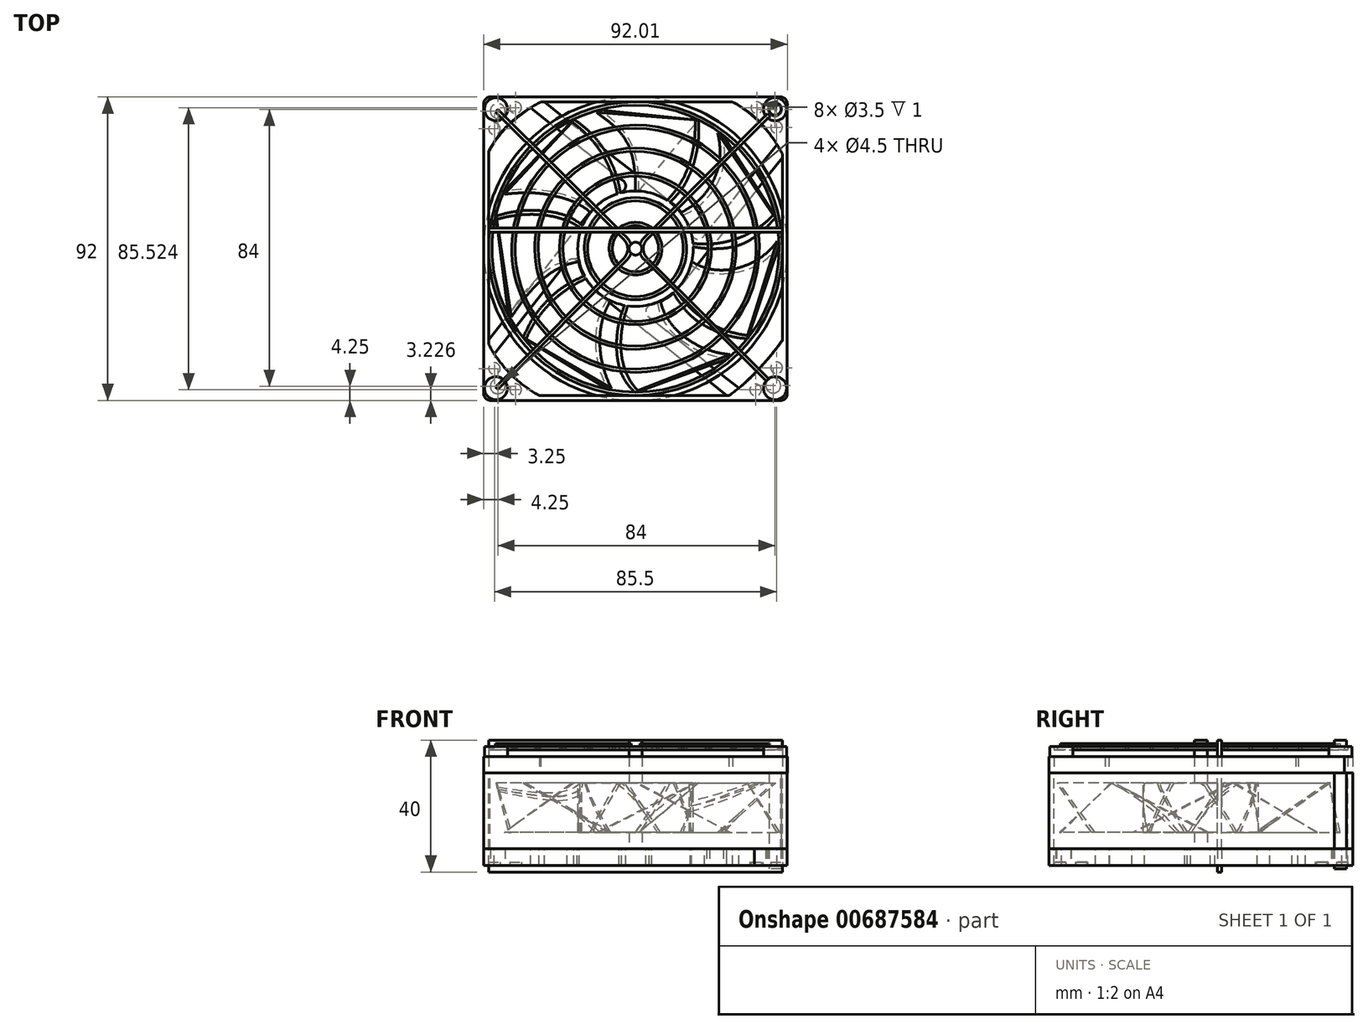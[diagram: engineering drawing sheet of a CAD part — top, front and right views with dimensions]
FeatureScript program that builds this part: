
annotation { "Feature Type Name" : "Feature", "Feature Type Description" : "" }
export const myFeature = defineFeature(function(context is Context, id is Id, definition is map)
    precondition{}
    {
        {
            var Q0;
            Q0=qCreatedBy(makeId("Top.planeOp"),FACE);
            var sketch = newSketch(context, id + "F0", { "sketchPlane" : qUnion([Q0])});
            skCircle(sketch, "E0", {"center": v(0, 0) * mm, "radius": 17.5 * mm});
            skFitSpline(sketch, "E1", {"points": [v(0, 17.5) * mm, v(-2.1, 31.24) * mm, v(-11.86, 41.33) * mm], "startDerivative": vector(0, 25.96) * mm, "endDerivative": vector(-26.51, 18.2) * mm});
            skFitSpline(sketch, "E2", {"points": [v(-13.7, 10.9) * mm, v(-25.14, 16.14) * mm, v(-39.7, 16.51) * mm], "startDerivative": vector(-17.17, 18.07) * mm, "endDerivative": vector(-36.07, -4.22) * mm});
            skFitSpline(sketch, "E3", {"points": [v(-17.05, -3.92) * mm, v(-37.64, -20.79) * mm], "startDerivative": vector(-28.13, -4.14) * mm, "endDerivative": vector(-14.48, -22.43) * mm});
            skFitSpline(sketch, "E4", {"points": [v(-7.55, -15.79) * mm, v(-7.23, -42.39) * mm], "startDerivative": vector(-14.78, -23.74) * mm, "endDerivative": vector(12.49, -22.98) * mm});
            skFitSpline(sketch, "E5", {"points": [v(7.55, -15.79) * mm, v(28.62, -32.1) * mm], "startDerivative": vector(6.16, -28.74) * mm, "endDerivative": vector(26.76, -2.2) * mm});
            skFitSpline(sketch, "E6", {"points": [v(17.05, -3.92) * mm, v(42.94, 2.35) * mm], "startDerivative": vector(28.81, -18.04) * mm, "endDerivative": vector(12.95, 20.22) * mm});
            skFitSpline(sketch, "E7", {"points": [v(13.7, 10.9) * mm, v(24.9, 35.05) * mm], "startDerivative": vector(22.05, 10.85) * mm, "endDerivative": vector(-8.83, 36.13) * mm});
            skFitSpline(sketch, "E8.0", {"points": [v(14.13, 10) * mm, v(16.05, 10.95) * mm, v(19.82, 13.47) * mm, v(24.37, 19.05) * mm, v(26.92, 26.33) * mm, v(26.64, 32.16) * mm, v(25.88, 35.29) * mm]});
            skFitSpline(sketch, "E9.0", {"points": [v(16.52, -4.77) * mm, v(17.8, -5.57) * mm, v(20.42, -6.78) * mm, v(24.46, -7.57) * mm, v(28.47, -7.48) * mm, v(33.6, -6.35) * mm, v(39.34, -3.38) * mm, v(42.62, 0) * mm, v(43.78, 1.8) * mm]});
            skFitSpline(sketch, "E10.0", {"points": [v(6.57, -16) * mm, v(7.12, -18.53) * mm, v(9.27, -23.13) * mm, v(14.71, -28.36) * mm, v(21.44, -31.83) * mm, v(26.21, -32.9) * mm, v(28.54, -33.1) * mm]});
            skFitSpline(sketch, "E11.0", {"points": [v(-8.4, -15.26) * mm, v(-9.7, -17.34) * mm, v(-11.48, -21.9) * mm, v(-12.1, -29.23) * mm, v(-10.94, -36.49) * mm, v(-9.2, -40.88) * mm, v(-8.11, -42.86) * mm]});
            skFitSpline(sketch, "E12.0", {"points": [v(-17.2, -2.94) * mm, v(-19.67, -3.3) * mm, v(-24.2, -4.9) * mm, v(-29.9, -9.15) * mm, v(-34.63, -14.5) * mm, v(-37.27, -18.36) * mm, v(-38.48, -20.24) * mm]});
            skFitSpline(sketch, "E13.0", {"points": [v(-12.97, 11.59) * mm, v(-13.75, 12.41) * mm, v(-15.56, 13.83) * mm, v(-18.2, 15.12) * mm, v(-20.4, 15.93) * mm, v(-22.1, 16.45) * mm, v(-23.77, 16.87) * mm, v(-25.42, 17.22) * mm, v(-27.03, 17.51) * mm, v(-29.17, 17.8) * mm, v(-31.91, 18) * mm, v(-35.52, 17.93) * mm, v(-38.3, 17.69) * mm, v(-39.82, 17.5) * mm]});
            skFitSpline(sketch, "E14.0", {"points": [v(1, 17.5) * mm, v(1, 18.6) * mm, v(0.97, 20.9) * mm, v(0.7, 24.59) * mm, v(0.16, 27.65) * mm, v(-0.52, 30) * mm, v(-1.18, 31.7) * mm, v(-2, 33.28) * mm, v(-3.3, 35.25) * mm, v(-5.25, 37.46) * mm, v(-8.05, 39.87) * mm, v(-10.18, 41.4) * mm, v(-11.3, 42.16) * mm]});
            skLineSegment(sketch, "E15", {"start": v(-11.3, 42.16) * mm, "end": v(-11.86, 41.33) * mm});
            skLineSegment(sketch, "E16", {"start": v(-39.82, 17.5) * mm, "end": v(-39.7, 16.51) * mm});
            skLineSegment(sketch, "E17", {"start": v(25.88, 35.29) * mm, "end": v(24.9, 35.05) * mm});
            skLineSegment(sketch, "E18", {"start": v(43.78, 1.8) * mm, "end": v(42.94, 2.35) * mm});
            skLineSegment(sketch, "E19", {"start": v(28.62, -32.1) * mm, "end": v(28.54, -33.1) * mm});
            skLineSegment(sketch, "E20", {"start": v(-8.11, -42.86) * mm, "end": v(-7.23, -42.39) * mm});
            skLineSegment(sketch, "E21", {"start": v(-38.48, -20.24) * mm, "end": v(-37.64, -20.79) * mm});
            skLineSegment(sketch, "E22", {"start": v(1, 17.5) * mm, "end": v(1, 17.47) * mm});
            skLineSegment(sketch, "E23", {"start": v(1, 17.47) * mm, "end": v(1, 17.47) * mm});
            skSolve(sketch);
        }
        {
            var Q0;
            Q0=qCreatedBy(makeId("Top.planeOp"),FACE);
            cPlane(context, id + "F1", {"entities" : qUnion([Q0]), "cplaneType" : CPlaneType.OFFSET, "offset" : 15 * mm, "width" : 150 * mm, "height" : 150 * mm});
        }
        {
            var Q0;
            Q0=qCreatedBy(id+"F1.planeOp",FACE);
            var sketch = newSketch(context, id + "F2", { "sketchPlane" : qUnion([Q0])});
            skCircle(sketch, "E24", {"center": v(0, 0) * mm, "radius": 17.5 * mm});
            skPoint(sketch, "E25", {"position": v(-17.05, -3.94) * mm});
            skPoint(sketch, "E26", {"position": v(-13.7, 10.9) * mm});
            skFitSpline(sketch, "E27", {"points": [v(-16.42, 6.06) * mm, v(-42.07, 8.89) * mm], "startDerivative": vector(-19.69, 14.9) * mm, "endDerivative": vector(-25.42, -7.54) * mm});
            skFitSpline(sketch, "E28", {"points": [v(-5.5, 16.61) * mm, v(-19.24, 38.45) * mm], "startDerivative": vector(-5.34, 25.3) * mm, "endDerivative": vector(-24.96, 18.67) * mm});
            skFitSpline(sketch, "E29", {"points": [v(9.58, 14.64) * mm, v(18.05, 39.03) * mm], "startDerivative": vector(20.74, 21.13) * mm, "endDerivative": vector(-0.95, 24.65) * mm});
            skFitSpline(sketch, "E30", {"points": [v(17.42, 1.62) * mm, v(41.76, 10.23) * mm], "startDerivative": vector(29.36, -3.55) * mm, "endDerivative": vector(17.15, 18.36) * mm});
            skFitSpline(sketch, "E31", {"points": [v(12.12, -12.62) * mm, v(34.02, -26.3) * mm], "startDerivative": vector(14.06, -21.25) * mm, "endDerivative": vector(28.38, -2.91) * mm});
            skFitSpline(sketch, "E32", {"points": [v(-2.33, -17.34) * mm, v(0.67, -43) * mm], "startDerivative": vector(-8.35, -22.6) * mm, "endDerivative": vector(20.25, -21.14) * mm});
            skFitSpline(sketch, "E33", {"points": [v(-14.96, -9.07) * mm, v(-33.19, -27.34) * mm], "startDerivative": vector(-27.43, -12.67) * mm, "endDerivative": vector(-11, -23.73) * mm});
            skFitSpline(sketch, "E34.0", {"points": [v(-4.52, 16.82) * mm, v(-4.97, 18.97) * mm, v(-6.12, 23.12) * mm, v(-8.85, 28.95) * mm, v(-12.85, 34.35) * mm, v(-16.52, 37.67) * mm, v(-18.64, 39.26) * mm]});
            skFitSpline(sketch, "E35.0", {"points": [v(10.3, 13.94) * mm, v(12.09, 15.76) * mm, v(15.01, 19.68) * mm, v(17.72, 26.07) * mm, v(19.02, 32.64) * mm, v(19.13, 36.97) * mm, v(19.05, 39.06) * mm]});
            skFitSpline(sketch, "E36.0", {"points": [v(17.3, 0.63) * mm, v(22.36, 0.02) * mm, v(32, 1.3) * mm, v(39.53, 6.38) * mm, v(42.5, 9.55) * mm]});
            skFitSpline(sketch, "E37.0", {"points": [v(11.29, -13.17) * mm, v(13.7, -16.83) * mm, v(18.5, -21.74) * mm, v(26.8, -25.94) * mm, v(31.47, -27.04) * mm, v(33.92, -27.3) * mm]});
            skFitSpline(sketch, "E38.0", {"points": [v(-3.27, -17) * mm, v(-3.98, -18.94) * mm, v(-5.18, -23.26) * mm, v(-5.71, -30.4) * mm, v(-4.4, -37.55) * mm, v(-1.84, -41.82) * mm, v(-0.05, -43.69) * mm]});
            skFitSpline(sketch, "E39.0", {"points": [v(-15.38, -8.17) * mm, v(-17.72, -9.25) * mm, v(-21.93, -11.66) * mm, v(-27.02, -16.01) * mm, v(-31.06, -21.08) * mm, v(-33.16, -24.9) * mm, v(-34.1, -26.92) * mm]});
            skFitSpline(sketch, "E40.0", {"points": [v(-15.82, 6.85) * mm, v(-17.55, 8.17) * mm, v(-21.54, 10.17) * mm, v(-28.39, 11.51) * mm, v(-35.55, 11.4) * mm, v(-40.18, 10.5) * mm, v(-42.36, 9.84) * mm]});
            skLineSegment(sketch, "E41", {"start": v(-42.36, 9.84) * mm, "end": v(-42.07, 8.89) * mm});
            skLineSegment(sketch, "E42", {"start": v(-18.64, 39.26) * mm, "end": v(-19.24, 38.45) * mm});
            skLineSegment(sketch, "E43", {"start": v(18.05, 39.03) * mm, "end": v(19.05, 39.06) * mm});
            skLineSegment(sketch, "E44", {"start": v(41.76, 10.23) * mm, "end": v(42.5, 9.55) * mm});
            skLineSegment(sketch, "E45", {"start": v(34.02, -26.3) * mm, "end": v(33.92, -27.3) * mm});
            skLineSegment(sketch, "E46", {"start": v(-0.05, -43.69) * mm, "end": v(0.67, -43) * mm});
            skLineSegment(sketch, "E47", {"start": v(-34.1, -26.92) * mm, "end": v(-33.19, -27.34) * mm});
            skSolve(sketch);
        }
        {
            var Q0;
            {var subQ0=sQuery(id+"F0.wireOp",EDGE,"E0");var subQ8=makeQuery(id+"F0.imprint","INTERSECT",VERTEX,{"derivedFrom":[subQ0,sQuery(id+"F0.wireOp",EDGE,"E7")]});Q0=makeQuery(id+"F0.imprint","IMPRINT",FACE,{"disambiguationData":[TD([[makeQuery(id+"F0.imprint","IMPRINT",EDGE,{"disambiguationData":[TD([[subQ8,1.0]])],"derivedFrom":subQ0}),1.0]])]});}
            var Q1;
            {var subQ0=sQuery(id+"F2.wireOp",EDGE,"E24");var subQ8=makeQuery(id+"F2.imprint","INTERSECT",VERTEX,{"derivedFrom":[subQ0,sQuery(id+"F2.wireOp",EDGE,"E30")]});Q1=makeQuery(id+"F2.imprint","IMPRINT",FACE,{"disambiguationData":[TD([[makeQuery(id+"F2.imprint","IMPRINT",EDGE,{"disambiguationData":[TD([[subQ8,1.0]])],"derivedFrom":subQ0}),1.0]])]});}
            loft(context, id + "F3", {"sheetProfilesArray" : [{ "sheetProfileEntities" : qUnion([Q0]) }, { "sheetProfileEntities" : qUnion([Q1]) }]});
        }
        {
            var Q1;
            {var subQ0=sQuery(id+"F2.wireOp",EDGE,"E27");Q1=makeQuery(id+"F2.imprint","IMPRINT",FACE,{"disambiguationData":[TD([[makeQuery(id+"F2.imprint","IMPRINT",EDGE,{"derivedFrom":subQ0}),-1.0]])]});}
            var Q2;
            {var subQ0=sQuery(id+"F0.wireOp",EDGE,"E3");Q2=makeQuery(id+"F0.imprint","IMPRINT",FACE,{"disambiguationData":[TD([[makeQuery(id+"F0.imprint","IMPRINT",EDGE,{"derivedFrom":subQ0}),-1.0]])]});}
            loft(context, id + "F4", {"operationType" : NewBodyOperationType.ADD, "sheetProfilesArray" : [{ "sheetProfileEntities" : qUnion([Q1]) }, { "sheetProfileEntities" : qUnion([Q2]) }]});
        }
        {
            var Q1;
            {var subQ0=sQuery(id+"F2.wireOp",EDGE,"E28");Q1=makeQuery(id+"F2.imprint","IMPRINT",FACE,{"disambiguationData":[TD([[makeQuery(id+"F2.imprint","IMPRINT",EDGE,{"derivedFrom":subQ0}),-1.0]])]});}
            var Q2;
            {var subQ0=sQuery(id+"F0.wireOp",EDGE,"E2");Q2=makeQuery(id+"F0.imprint","IMPRINT",FACE,{"disambiguationData":[TD([[makeQuery(id+"F0.imprint","IMPRINT",EDGE,{"derivedFrom":subQ0}),-1.0]])]});}
            loft(context, id + "F5", {"operationType" : NewBodyOperationType.ADD, "sheetProfilesArray" : [{ "sheetProfileEntities" : qUnion([Q1]) }, { "sheetProfileEntities" : qUnion([Q2]) }]});
        }
        {
            var Q1;
            {var subQ0=sQuery(id+"F2.wireOp",EDGE,"E33");Q1=makeQuery(id+"F2.imprint","IMPRINT",FACE,{"disambiguationData":[TD([[makeQuery(id+"F2.imprint","IMPRINT",EDGE,{"derivedFrom":subQ0}),-1.0]])]});}
            var Q2;
            {var subQ0=sQuery(id+"F0.wireOp",EDGE,"E4");Q2=makeQuery(id+"F0.imprint","IMPRINT",FACE,{"disambiguationData":[TD([[makeQuery(id+"F0.imprint","IMPRINT",EDGE,{"derivedFrom":subQ0}),-1.0]])]});}
            loft(context, id + "F6", {"operationType" : NewBodyOperationType.ADD, "sheetProfilesArray" : [{ "sheetProfileEntities" : qUnion([Q1]) }, { "sheetProfileEntities" : qUnion([Q2]) }]});
        }
        {
            var Q1;
            {var subQ0=sQuery(id+"F0.wireOp",EDGE,"E1");Q1=makeQuery(id+"F0.imprint","IMPRINT",FACE,{"disambiguationData":[TD([[makeQuery(id+"F0.imprint","IMPRINT",EDGE,{"derivedFrom":subQ0}),-1.0]])]});}
            var Q2;
            {var subQ0=sQuery(id+"F2.wireOp",EDGE,"E29");Q2=makeQuery(id+"F2.imprint","IMPRINT",FACE,{"disambiguationData":[TD([[makeQuery(id+"F2.imprint","IMPRINT",EDGE,{"derivedFrom":subQ0}),-1.0]])]});}
            loft(context, id + "F7", {"operationType" : NewBodyOperationType.ADD, "sheetProfilesArray" : [{ "sheetProfileEntities" : qUnion([Q1]) }, { "sheetProfileEntities" : qUnion([Q2]) }]});
        }
        {
            var Q1;
            {var subQ0=sQuery(id+"F0.wireOp",EDGE,"E7");Q1=makeQuery(id+"F0.imprint","IMPRINT",FACE,{"disambiguationData":[TD([[makeQuery(id+"F0.imprint","IMPRINT",EDGE,{"derivedFrom":subQ0}),-1.0]])]});}
            var Q2;
            {var subQ0=sQuery(id+"F2.wireOp",EDGE,"E30");Q2=makeQuery(id+"F2.imprint","IMPRINT",FACE,{"disambiguationData":[TD([[makeQuery(id+"F2.imprint","IMPRINT",EDGE,{"derivedFrom":subQ0}),-1.0]])]});}
            loft(context, id + "F8", {"operationType" : NewBodyOperationType.ADD, "sheetProfilesArray" : [{ "sheetProfileEntities" : qUnion([Q1]) }, { "sheetProfileEntities" : qUnion([Q2]) }]});
        }
        {
            var Q1;
            {var subQ0=sQuery(id+"F0.wireOp",EDGE,"E6");Q1=makeQuery(id+"F0.imprint","IMPRINT",FACE,{"disambiguationData":[TD([[makeQuery(id+"F0.imprint","IMPRINT",EDGE,{"derivedFrom":subQ0}),-1.0]])]});}
            var Q2;
            {var subQ0=sQuery(id+"F2.wireOp",EDGE,"E31");Q2=makeQuery(id+"F2.imprint","IMPRINT",FACE,{"disambiguationData":[TD([[makeQuery(id+"F2.imprint","IMPRINT",EDGE,{"derivedFrom":subQ0}),-1.0]])]});}
            loft(context, id + "F9", {"operationType" : NewBodyOperationType.ADD, "sheetProfilesArray" : [{ "sheetProfileEntities" : qUnion([Q1]) }, { "sheetProfileEntities" : qUnion([Q2]) }]});
        }
        {
            var Q1;
            {var subQ0=sQuery(id+"F0.wireOp",EDGE,"E5");Q1=makeQuery(id+"F0.imprint","IMPRINT",FACE,{"disambiguationData":[TD([[makeQuery(id+"F0.imprint","IMPRINT",EDGE,{"derivedFrom":subQ0}),-1.0]])]});}
            var Q2;
            {var subQ0=sQuery(id+"F2.wireOp",EDGE,"E32");Q2=makeQuery(id+"F2.imprint","IMPRINT",FACE,{"disambiguationData":[TD([[makeQuery(id+"F2.imprint","IMPRINT",EDGE,{"derivedFrom":subQ0}),-1.0]])]});}
            loft(context, id + "F10", {"operationType" : NewBodyOperationType.ADD, "sheetProfilesArray" : [{ "sheetProfileEntities" : qUnion([Q1]) }, { "sheetProfileEntities" : qUnion([Q2]) }]});
        }
        {
            var Q0;
            Q0=qCreatedBy(makeId("Top.planeOp"),FACE);
            cPlane(context, id + "F11", {"entities" : qUnion([Q0]), "cplaneType" : CPlaneType.OFFSET, "offset" : 5 * mm, "oppositeDirection" : true, "width" : 150 * mm, "height" : 150 * mm});
        }
        {
            var Q0;
            Q0=qCreatedBy(id+"F11.planeOp",FACE);
            var sketch = newSketch(context, id + "F12", { "sketchPlane" : qUnion([Q0])});
            skArc(sketch, "E48", {"start": v(4.24, -17.24) * mm, "mid": v(9.6, -14.93) * mm, "end": v(13.92, -11.01) * mm});
            skLineSegment(sketch, "E49", {"start": v(36, -46) * mm, "end": v(44.08, -45.69) * mm});
            skLineSegment(sketch, "E50", {"start": v(46, -43.69) * mm, "end": v(46, 44) * mm});
            skLineSegment(sketch, "E51", {"start": v(36, -46) * mm, "end": v(-44, -46) * mm});
            skLineSegment(sketch, "E52", {"start": v(-46, -44) * mm, "end": v(-46, 44) * mm});
            skLineSegment(sketch, "E53", {"start": v(-44, 46) * mm, "end": v(26, 46) * mm});
            skPoint(sketch, "E54.endSnap0", {"position": v(0, 46) * mm});
            skLineSegment(sketch, "E55", {"start": v(27.65, -44.5) * mm, "end": v(-11.01, -13.92) * mm});
            skLineSegment(sketch, "E56", {"start": v(31.31, -42.3) * mm, "end": v(3.54, -20.33) * mm});
            skArc(sketch, "E57", {"start": v(4.9, -17.06) * mm, "mid": v(3.11, -18.68) * mm, "end": v(4.2, -20.84) * mm});
            skLineSegment(sketch, "E58", {"start": v(44.5, 27.65) * mm, "end": v(13.92, -11.01) * mm});
            skArc(sketch, "E59", {"start": v(17.02, 5.05) * mm, "mid": v(18.63, 2.88) * mm, "end": v(20.93, 4.3) * mm});
            skArc(sketch, "E60.trimOffspring", {"start": v(17.36, 3.72) * mm, "mid": v(15.07, 9.37) * mm, "end": v(11.01, 13.92) * mm});
            skLineSegment(sketch, "E61", {"start": v(-27.65, 44.5) * mm, "end": v(11.01, 13.92) * mm});
            skLineSegment(sketch, "E62", {"start": v(-31.83, 42.7) * mm, "end": v(-3.31, 20.15) * mm});
            skPoint(sketch, "E63.orphan", {"position": v(-32, 47.94) * mm});
            skArc(sketch, "E64", {"start": v(-4.95, 17.05) * mm, "mid": v(-3, 18.71) * mm, "end": v(-4.3, 20.92) * mm});
            skArc(sketch, "E65.trimOffspring", {"start": v(-4.03, 17.29) * mm, "mid": v(-9.5, 14.99) * mm, "end": v(-13.92, 11.01) * mm});
            skLineSegment(sketch, "E66", {"start": v(-44.5, -27.65) * mm, "end": v(-13.92, 11.01) * mm});
            skLineSegment(sketch, "E67", {"start": v(-42.8, -31.95) * mm, "end": v(-20.44, -3.69) * mm});
            skPoint(sketch, "E68.orphan", {"position": v(-47.94, -32) * mm});
            skArc(sketch, "E69", {"start": v(-17.06, -4.88) * mm, "mid": v(-18.63, -3.16) * mm, "end": v(-20.77, -4.1) * mm});
            skArc(sketch, "E70.trimOffspring", {"start": v(-17.21, -4.33) * mm, "mid": v(-14.9, -9.64) * mm, "end": v(-11.01, -13.92) * mm});
            skPoint(sketch, "E71.orphan", {"position": v(-46, 0) * mm});
            skPoint(sketch, "E54.end.orphan", {"position": v(0, 46) * mm});
            skLineSegment(sketch, "E72.0", {"start": v(44.5, -27.75) * mm, "end": v(44.5, 27.65) * mm});
            skLineSegment(sketch, "E72.1", {"start": v(-27.65, 44.5) * mm, "end": v(29.37, 44.5) * mm});
            skLineSegment(sketch, "E72.2", {"start": v(-44.5, -27.65) * mm, "end": v(-44.5, 29.38) * mm});
            skLineSegment(sketch, "E72.3", {"start": v(0, -44.5) * mm, "end": v(-29.19, -44.5) * mm});
            skLineSegment(sketch, "E73", {"start": v(-46, 44) * mm, "end": v(-46, 26) * mm});
            skLineSegment(sketch, "E74", {"start": v(-44, 46) * mm, "end": v(-29.55, 46) * mm});
            skFitSpline(sketch, "E75", {"points": [v(-46, 26) * mm, v(-26, 46) * mm], "startDerivative": vector(10.96, 29.27) * mm, "endDerivative": vector(25.62, 12.75) * mm});
            skPoint(sketch, "E76.orphan", {"position": v(-36, 46) * mm});
            skPoint(sketch, "E77.visualSharp", {"position": v(-46, 46) * mm});
            skArc(sketch, "E77.filletArc", {"start": v(-44, 46) * mm, "mid": v(-45.41, 45.41) * mm, "end": v(-46, 44) * mm});
            skPoint(sketch, "E78.visualSharp", {"position": v(-46, -46) * mm});
            skArc(sketch, "E78.filletArc", {"start": v(-46, -44) * mm, "mid": v(-45.41, -45.41) * mm, "end": v(-44, -46) * mm});
            skLineSegment(sketch, "E79", {"start": v(0, -44.5) * mm, "end": v(27.65, -44.5) * mm});
            skPoint(sketch, "E80.visualSharp", {"position": v(46, -45.61) * mm});
            skArc(sketch, "E80.filletArc", {"start": v(44.08, -45.69) * mm, "mid": v(45.44, -45.08) * mm, "end": v(46, -43.69) * mm});
            skPoint(sketch, "E81.visualSharp", {"position": v(46, 46) * mm});
            skArc(sketch, "E81.filletArc", {"start": v(46, 44) * mm, "mid": v(45.41, 45.41) * mm, "end": v(44, 46) * mm});
            skPoint(sketch, "E82.orphan", {"position": v(-46, -36) * mm});
            skLineSegment(sketch, "E83", {"start": v(-46, -44) * mm, "end": v(-46, -26) * mm});
            skLineSegment(sketch, "E84", {"start": v(-44, -46) * mm, "end": v(-26, -46) * mm});
            skFitSpline(sketch, "E85", {"points": [v(-46, -26) * mm, v(-26, -46) * mm], "startDerivative": vector(11.48, -26.33) * mm, "endDerivative": vector(28, -11.54) * mm});
            skLineSegment(sketch, "E86", {"start": v(46, -43.69) * mm, "end": v(46, -25.61) * mm});
            skLineSegment(sketch, "E87", {"start": v(44.08, -45.69) * mm, "end": v(36, -46) * mm});
            skFitSpline(sketch, "E88", {"points": [v(26, -46.39) * mm, v(46, -25.61) * mm], "startDerivative": vector(23.59, 16.36) * mm, "endDerivative": vector(17.03, 24.93) * mm});
            skPoint(sketch, "E89.orphan", {"position": v(36, -46) * mm});
            skLineSegment(sketch, "E90", {"start": v(44, 46) * mm, "end": v(26, 46) * mm});
            skLineSegment(sketch, "E91", {"start": v(46, 44) * mm, "end": v(46, 26) * mm});
            skFitSpline(sketch, "E92", {"points": [v(26, 46) * mm, v(46, 26) * mm], "startDerivative": vector(29.17, -10.7) * mm, "endDerivative": vector(10.2, -22.47) * mm});
            skLineSegment(sketch, "E93.trimOffspring", {"start": v(42.91, 31.62) * mm, "end": v(19.98, 3.1) * mm});
            skPoint(sketch, "E94.start.orphan", {"position": v(46, 36) * mm});
            skSolve(sketch);
        }
        {
            var Q0;
            {var subQ24=sQuery(id+"F12.wireOp",EDGE,"E55");Q0=makeQuery(id+"F12.imprint","IMPRINT",FACE,{"disambiguationData":[TD([[makeQuery(id+"F12.imprint","IMPRINT",EDGE,{"derivedFrom":subQ24}),-1.0]])]});}
            extrude(context, id + "F13", {"entities" : qUnion([Q0]), "operationType" : NewBodyOperationType.ADD, "oppositeDirection" : true, "depth" : 5 * mm, "offsetDistance" : 25 * mm});
        }
        {
            var Q0;
            Q0 = qSketchRegion(id + "F12", true);
            extrude(context, id + "F14", {"entities" : qUnion([Q0]), "oppositeDirection" : true, "depth" : 5 * mm, "offsetDistance" : 25 * mm});
        }
        {
            var Q0;
            Q0=makeQuery(id+"F13.opExtrude","CAP_FACE",FACE,{"disambiguationData":[OSD([sQuery(id+"F12.wireOp",EDGE,"E48"),sQuery(id+"F12.wireOp",EDGE,"E50"),sQuery(id+"F12.wireOp",EDGE,"E51"),sQuery(id+"F12.wireOp",EDGE,"E52"),sQuery(id+"F12.wireOp",EDGE,"E53"),sQuery(id+"F12.wireOp",EDGE,"E55"),sQuery(id+"F12.wireOp",EDGE,"E56"),sQuery(id+"F12.wireOp",EDGE,"E57"),sQuery(id+"F12.wireOp",EDGE,"E58"),sQuery(id+"F12.wireOp",EDGE,"E59"),sQuery(id+"F12.wireOp",EDGE,"E60.trimOffspring"),sQuery(id+"F12.wireOp",EDGE,"E61"),sQuery(id+"F12.wireOp",EDGE,"E62"),sQuery(id+"F12.wireOp",EDGE,"E64"),sQuery(id+"F12.wireOp",EDGE,"E65.trimOffspring"),sQuery(id+"F12.wireOp",EDGE,"E66"),sQuery(id+"F12.wireOp",EDGE,"E67"),sQuery(id+"F12.wireOp",EDGE,"E69"),sQuery(id+"F12.wireOp",EDGE,"E70.trimOffspring"),sQuery(id+"F12.wireOp",EDGE,"E72.0"),sQuery(id+"F12.wireOp",EDGE,"E72.1"),sQuery(id+"F12.wireOp",EDGE,"E72.2"),sQuery(id+"F12.wireOp",EDGE,"E72.3"),sQuery(id+"F12.wireOp",EDGE,"E73"),sQuery(id+"F12.wireOp",EDGE,"E74"),sQuery(id+"F12.wireOp",EDGE,"E75"),sQuery(id+"F12.wireOp",EDGE,"E77.filletArc"),sQuery(id+"F12.wireOp",EDGE,"E78.filletArc"),sQuery(id+"F12.wireOp",EDGE,"E79"),sQuery(id+"F12.wireOp",EDGE,"E80.filletArc"),sQuery(id+"F12.wireOp",EDGE,"E81.filletArc"),sQuery(id+"F12.wireOp",EDGE,"E83"),sQuery(id+"F12.wireOp",EDGE,"E84"),sQuery(id+"F12.wireOp",EDGE,"E85"),sQuery(id+"F12.wireOp",EDGE,"E86"),sQuery(id+"F12.wireOp",EDGE,"E87"),sQuery(id+"F12.wireOp",EDGE,"E90"),sQuery(id+"F12.wireOp",EDGE,"E91"),sQuery(id+"F12.wireOp",EDGE,"E92"),sQuery(id+"F12.wireOp",EDGE,"E93.trimOffspring"),sQuery(id+"F12.wireOp",EDGE,"E88")])],"isStart":false});
            var sketch = newSketch(context, id + "F15", { "sketchPlane" : qUnion([Q0])});
            skCircle(sketch, "E95", {"center": v(-41.75, -41.75) * mm, "radius": 2.25 * mm});
            skSolve(sketch);
        }
        {
            var Q0;
            Q0 = qSketchRegion(id + "F15", true);
            extrude(context, id + "F16", {"entities" : qUnion([Q0]), "operationType" : NewBodyOperationType.REMOVE, "endBound" : BoundingType.THROUGH_ALL, "oppositeDirection" : true, "depth" : 25 * mm, "offsetDistance" : 25 * mm});
        }
        {
            var Q0;
            Q0=makeQuery(id+"F13.opExtrude","CAP_FACE",FACE,{"disambiguationData":[OSD([sQuery(id+"F12.wireOp",EDGE,"E48"),sQuery(id+"F12.wireOp",EDGE,"E50"),sQuery(id+"F12.wireOp",EDGE,"E51"),sQuery(id+"F12.wireOp",EDGE,"E52"),sQuery(id+"F12.wireOp",EDGE,"E53"),sQuery(id+"F12.wireOp",EDGE,"E55"),sQuery(id+"F12.wireOp",EDGE,"E56"),sQuery(id+"F12.wireOp",EDGE,"E57"),sQuery(id+"F12.wireOp",EDGE,"E58"),sQuery(id+"F12.wireOp",EDGE,"E59"),sQuery(id+"F12.wireOp",EDGE,"E60.trimOffspring"),sQuery(id+"F12.wireOp",EDGE,"E61"),sQuery(id+"F12.wireOp",EDGE,"E62"),sQuery(id+"F12.wireOp",EDGE,"E64"),sQuery(id+"F12.wireOp",EDGE,"E65.trimOffspring"),sQuery(id+"F12.wireOp",EDGE,"E66"),sQuery(id+"F12.wireOp",EDGE,"E67"),sQuery(id+"F12.wireOp",EDGE,"E69"),sQuery(id+"F12.wireOp",EDGE,"E70.trimOffspring"),sQuery(id+"F12.wireOp",EDGE,"E72.0"),sQuery(id+"F12.wireOp",EDGE,"E72.1"),sQuery(id+"F12.wireOp",EDGE,"E72.2"),sQuery(id+"F12.wireOp",EDGE,"E72.3"),sQuery(id+"F12.wireOp",EDGE,"E73"),sQuery(id+"F12.wireOp",EDGE,"E74"),sQuery(id+"F12.wireOp",EDGE,"E75"),sQuery(id+"F12.wireOp",EDGE,"E77.filletArc"),sQuery(id+"F12.wireOp",EDGE,"E78.filletArc"),sQuery(id+"F12.wireOp",EDGE,"E79"),sQuery(id+"F12.wireOp",EDGE,"E80.filletArc"),sQuery(id+"F12.wireOp",EDGE,"E81.filletArc"),sQuery(id+"F12.wireOp",EDGE,"E83"),sQuery(id+"F12.wireOp",EDGE,"E84"),sQuery(id+"F12.wireOp",EDGE,"E85"),sQuery(id+"F12.wireOp",EDGE,"E86"),sQuery(id+"F12.wireOp",EDGE,"E87"),sQuery(id+"F12.wireOp",EDGE,"E90"),sQuery(id+"F12.wireOp",EDGE,"E91"),sQuery(id+"F12.wireOp",EDGE,"E92"),sQuery(id+"F12.wireOp",EDGE,"E93.trimOffspring"),sQuery(id+"F12.wireOp",EDGE,"E88")])],"isStart":false});
            var sketch = newSketch(context, id + "F17", { "sketchPlane" : qUnion([Q0])});
            skCircle(sketch, "E96", {"center": v(-42.75, -36.34) * mm, "radius": 1.75 * mm});
            skSolve(sketch);
        }
        {
            var Q0;
            Q0 = qSketchRegion(id + "F17", true);
            extrude(context, id + "F18", {"entities" : qUnion([Q0]), "operationType" : NewBodyOperationType.REMOVE, "oppositeDirection" : true, "depth" : 1 * mm, "offsetDistance" : 25 * mm});
        }
        {
            var Q0;
            Q0=makeQuery(id+"F13.opExtrude","CAP_FACE",FACE,{"disambiguationData":[OSD([sQuery(id+"F12.wireOp",EDGE,"E48"),sQuery(id+"F12.wireOp",EDGE,"E50"),sQuery(id+"F12.wireOp",EDGE,"E51"),sQuery(id+"F12.wireOp",EDGE,"E52"),sQuery(id+"F12.wireOp",EDGE,"E53"),sQuery(id+"F12.wireOp",EDGE,"E55"),sQuery(id+"F12.wireOp",EDGE,"E56"),sQuery(id+"F12.wireOp",EDGE,"E57"),sQuery(id+"F12.wireOp",EDGE,"E58"),sQuery(id+"F12.wireOp",EDGE,"E59"),sQuery(id+"F12.wireOp",EDGE,"E60.trimOffspring"),sQuery(id+"F12.wireOp",EDGE,"E61"),sQuery(id+"F12.wireOp",EDGE,"E62"),sQuery(id+"F12.wireOp",EDGE,"E64"),sQuery(id+"F12.wireOp",EDGE,"E65.trimOffspring"),sQuery(id+"F12.wireOp",EDGE,"E66"),sQuery(id+"F12.wireOp",EDGE,"E67"),sQuery(id+"F12.wireOp",EDGE,"E69"),sQuery(id+"F12.wireOp",EDGE,"E70.trimOffspring"),sQuery(id+"F12.wireOp",EDGE,"E72.0"),sQuery(id+"F12.wireOp",EDGE,"E72.1"),sQuery(id+"F12.wireOp",EDGE,"E72.2"),sQuery(id+"F12.wireOp",EDGE,"E72.3"),sQuery(id+"F12.wireOp",EDGE,"E73"),sQuery(id+"F12.wireOp",EDGE,"E74"),sQuery(id+"F12.wireOp",EDGE,"E75"),sQuery(id+"F12.wireOp",EDGE,"E77.filletArc"),sQuery(id+"F12.wireOp",EDGE,"E78.filletArc"),sQuery(id+"F12.wireOp",EDGE,"E79"),sQuery(id+"F12.wireOp",EDGE,"E80.filletArc"),sQuery(id+"F12.wireOp",EDGE,"E81.filletArc"),sQuery(id+"F12.wireOp",EDGE,"E83"),sQuery(id+"F12.wireOp",EDGE,"E84"),sQuery(id+"F12.wireOp",EDGE,"E85"),sQuery(id+"F12.wireOp",EDGE,"E86"),sQuery(id+"F12.wireOp",EDGE,"E87"),sQuery(id+"F12.wireOp",EDGE,"E90"),sQuery(id+"F12.wireOp",EDGE,"E91"),sQuery(id+"F12.wireOp",EDGE,"E92"),sQuery(id+"F12.wireOp",EDGE,"E93.trimOffspring"),sQuery(id+"F12.wireOp",EDGE,"E88")])],"isStart":false});
            var sketch = newSketch(context, id + "F19", { "sketchPlane" : qUnion([Q0])});
            skCircle(sketch, "E97", {"center": v(-36.34, -42.75) * mm, "radius": 1.75 * mm});
            skSolve(sketch);
        }
        {
            var Q0;
            Q0 = qSketchRegion(id + "F19", true);
            extrude(context, id + "F20", {"entities" : qUnion([Q0]), "operationType" : NewBodyOperationType.REMOVE, "oppositeDirection" : true, "depth" : 1 * mm, "offsetDistance" : 25 * mm});
        }
        {
            var Q0;
            Q0=makeQuery(id+"F13.opExtrude","CAP_FACE",FACE,{"disambiguationData":[OSD([sQuery(id+"F12.wireOp",EDGE,"E48"),sQuery(id+"F12.wireOp",EDGE,"E50"),sQuery(id+"F12.wireOp",EDGE,"E51"),sQuery(id+"F12.wireOp",EDGE,"E52"),sQuery(id+"F12.wireOp",EDGE,"E53"),sQuery(id+"F12.wireOp",EDGE,"E55"),sQuery(id+"F12.wireOp",EDGE,"E56"),sQuery(id+"F12.wireOp",EDGE,"E57"),sQuery(id+"F12.wireOp",EDGE,"E58"),sQuery(id+"F12.wireOp",EDGE,"E59"),sQuery(id+"F12.wireOp",EDGE,"E60.trimOffspring"),sQuery(id+"F12.wireOp",EDGE,"E61"),sQuery(id+"F12.wireOp",EDGE,"E62"),sQuery(id+"F12.wireOp",EDGE,"E64"),sQuery(id+"F12.wireOp",EDGE,"E65.trimOffspring"),sQuery(id+"F12.wireOp",EDGE,"E66"),sQuery(id+"F12.wireOp",EDGE,"E67"),sQuery(id+"F12.wireOp",EDGE,"E69"),sQuery(id+"F12.wireOp",EDGE,"E70.trimOffspring"),sQuery(id+"F12.wireOp",EDGE,"E72.0"),sQuery(id+"F12.wireOp",EDGE,"E72.1"),sQuery(id+"F12.wireOp",EDGE,"E72.2"),sQuery(id+"F12.wireOp",EDGE,"E72.3"),sQuery(id+"F12.wireOp",EDGE,"E73"),sQuery(id+"F12.wireOp",EDGE,"E74"),sQuery(id+"F12.wireOp",EDGE,"E75"),sQuery(id+"F12.wireOp",EDGE,"E77.filletArc"),sQuery(id+"F12.wireOp",EDGE,"E78.filletArc"),sQuery(id+"F12.wireOp",EDGE,"E79"),sQuery(id+"F12.wireOp",EDGE,"E80.filletArc"),sQuery(id+"F12.wireOp",EDGE,"E81.filletArc"),sQuery(id+"F12.wireOp",EDGE,"E83"),sQuery(id+"F12.wireOp",EDGE,"E84"),sQuery(id+"F12.wireOp",EDGE,"E85"),sQuery(id+"F12.wireOp",EDGE,"E86"),sQuery(id+"F12.wireOp",EDGE,"E87"),sQuery(id+"F12.wireOp",EDGE,"E90"),sQuery(id+"F12.wireOp",EDGE,"E91"),sQuery(id+"F12.wireOp",EDGE,"E92"),sQuery(id+"F12.wireOp",EDGE,"E93.trimOffspring"),sQuery(id+"F12.wireOp",EDGE,"E88")])],"isStart":false});
            var sketch = newSketch(context, id + "F21", { "sketchPlane" : qUnion([Q0])});
            skCircle(sketch, "E98", {"center": v(-41.75, 41.75) * mm, "radius": 2.25 * mm});
            skSolve(sketch);
        }
        {
            var Q0;
            Q0 = qSketchRegion(id + "F21", true);
            extrude(context, id + "F22", {"entities" : qUnion([Q0]), "operationType" : NewBodyOperationType.REMOVE, "endBound" : BoundingType.THROUGH_ALL, "oppositeDirection" : true, "depth" : 25 * mm, "offsetDistance" : 25 * mm});
        }
        {
            var Q0;
            Q0=makeQuery(id+"F13.opExtrude","CAP_FACE",FACE,{"disambiguationData":[OSD([sQuery(id+"F12.wireOp",EDGE,"E48"),sQuery(id+"F12.wireOp",EDGE,"E50"),sQuery(id+"F12.wireOp",EDGE,"E51"),sQuery(id+"F12.wireOp",EDGE,"E52"),sQuery(id+"F12.wireOp",EDGE,"E53"),sQuery(id+"F12.wireOp",EDGE,"E55"),sQuery(id+"F12.wireOp",EDGE,"E56"),sQuery(id+"F12.wireOp",EDGE,"E57"),sQuery(id+"F12.wireOp",EDGE,"E58"),sQuery(id+"F12.wireOp",EDGE,"E59"),sQuery(id+"F12.wireOp",EDGE,"E60.trimOffspring"),sQuery(id+"F12.wireOp",EDGE,"E61"),sQuery(id+"F12.wireOp",EDGE,"E62"),sQuery(id+"F12.wireOp",EDGE,"E64"),sQuery(id+"F12.wireOp",EDGE,"E65.trimOffspring"),sQuery(id+"F12.wireOp",EDGE,"E66"),sQuery(id+"F12.wireOp",EDGE,"E67"),sQuery(id+"F12.wireOp",EDGE,"E69"),sQuery(id+"F12.wireOp",EDGE,"E70.trimOffspring"),sQuery(id+"F12.wireOp",EDGE,"E72.0"),sQuery(id+"F12.wireOp",EDGE,"E72.1"),sQuery(id+"F12.wireOp",EDGE,"E72.2"),sQuery(id+"F12.wireOp",EDGE,"E72.3"),sQuery(id+"F12.wireOp",EDGE,"E73"),sQuery(id+"F12.wireOp",EDGE,"E74"),sQuery(id+"F12.wireOp",EDGE,"E75"),sQuery(id+"F12.wireOp",EDGE,"E77.filletArc"),sQuery(id+"F12.wireOp",EDGE,"E78.filletArc"),sQuery(id+"F12.wireOp",EDGE,"E79"),sQuery(id+"F12.wireOp",EDGE,"E80.filletArc"),sQuery(id+"F12.wireOp",EDGE,"E81.filletArc"),sQuery(id+"F12.wireOp",EDGE,"E83"),sQuery(id+"F12.wireOp",EDGE,"E84"),sQuery(id+"F12.wireOp",EDGE,"E85"),sQuery(id+"F12.wireOp",EDGE,"E86"),sQuery(id+"F12.wireOp",EDGE,"E87"),sQuery(id+"F12.wireOp",EDGE,"E90"),sQuery(id+"F12.wireOp",EDGE,"E91"),sQuery(id+"F12.wireOp",EDGE,"E92"),sQuery(id+"F12.wireOp",EDGE,"E93.trimOffspring"),sQuery(id+"F12.wireOp",EDGE,"E88")])],"isStart":false});
            var sketch = newSketch(context, id + "F23", { "sketchPlane" : qUnion([Q0])});
            skCircle(sketch, "E99", {"center": v(-42.75, 36.34) * mm, "radius": 1.75 * mm});
            skSolve(sketch);
        }
        {
            var Q0;
            Q0 = qSketchRegion(id + "F23", true);
            extrude(context, id + "F24", {"entities" : qUnion([Q0]), "operationType" : NewBodyOperationType.REMOVE, "oppositeDirection" : true, "depth" : 1 * mm, "offsetDistance" : 25 * mm});
        }
        {
            var Q0;
            Q0=makeQuery(id+"F13.opExtrude","CAP_FACE",FACE,{"disambiguationData":[OSD([sQuery(id+"F12.wireOp",EDGE,"E48"),sQuery(id+"F12.wireOp",EDGE,"E50"),sQuery(id+"F12.wireOp",EDGE,"E51"),sQuery(id+"F12.wireOp",EDGE,"E52"),sQuery(id+"F12.wireOp",EDGE,"E53"),sQuery(id+"F12.wireOp",EDGE,"E55"),sQuery(id+"F12.wireOp",EDGE,"E56"),sQuery(id+"F12.wireOp",EDGE,"E57"),sQuery(id+"F12.wireOp",EDGE,"E58"),sQuery(id+"F12.wireOp",EDGE,"E59"),sQuery(id+"F12.wireOp",EDGE,"E60.trimOffspring"),sQuery(id+"F12.wireOp",EDGE,"E61"),sQuery(id+"F12.wireOp",EDGE,"E62"),sQuery(id+"F12.wireOp",EDGE,"E64"),sQuery(id+"F12.wireOp",EDGE,"E65.trimOffspring"),sQuery(id+"F12.wireOp",EDGE,"E66"),sQuery(id+"F12.wireOp",EDGE,"E67"),sQuery(id+"F12.wireOp",EDGE,"E69"),sQuery(id+"F12.wireOp",EDGE,"E70.trimOffspring"),sQuery(id+"F12.wireOp",EDGE,"E72.0"),sQuery(id+"F12.wireOp",EDGE,"E72.1"),sQuery(id+"F12.wireOp",EDGE,"E72.2"),sQuery(id+"F12.wireOp",EDGE,"E72.3"),sQuery(id+"F12.wireOp",EDGE,"E73"),sQuery(id+"F12.wireOp",EDGE,"E74"),sQuery(id+"F12.wireOp",EDGE,"E75"),sQuery(id+"F12.wireOp",EDGE,"E77.filletArc"),sQuery(id+"F12.wireOp",EDGE,"E78.filletArc"),sQuery(id+"F12.wireOp",EDGE,"E79"),sQuery(id+"F12.wireOp",EDGE,"E80.filletArc"),sQuery(id+"F12.wireOp",EDGE,"E81.filletArc"),sQuery(id+"F12.wireOp",EDGE,"E83"),sQuery(id+"F12.wireOp",EDGE,"E84"),sQuery(id+"F12.wireOp",EDGE,"E85"),sQuery(id+"F12.wireOp",EDGE,"E86"),sQuery(id+"F12.wireOp",EDGE,"E87"),sQuery(id+"F12.wireOp",EDGE,"E90"),sQuery(id+"F12.wireOp",EDGE,"E91"),sQuery(id+"F12.wireOp",EDGE,"E92"),sQuery(id+"F12.wireOp",EDGE,"E93.trimOffspring"),sQuery(id+"F12.wireOp",EDGE,"E88")])],"isStart":false});
            var sketch = newSketch(context, id + "F25", { "sketchPlane" : qUnion([Q0])});
            skCircle(sketch, "E100", {"center": v(-36.34, 42.75) * mm, "radius": 1.75 * mm});
            skSolve(sketch);
        }
        {
            var Q0;
            Q0 = qSketchRegion(id + "F25", true);
            extrude(context, id + "F26", {"entities" : qUnion([Q0]), "operationType" : NewBodyOperationType.REMOVE, "oppositeDirection" : true, "depth" : 1 * mm, "offsetDistance" : 25 * mm});
        }
        {
            var Q0;
            Q0=makeQuery(id+"F13.opExtrude","CAP_FACE",FACE,{"disambiguationData":[OSD([sQuery(id+"F12.wireOp",EDGE,"E48"),sQuery(id+"F12.wireOp",EDGE,"E50"),sQuery(id+"F12.wireOp",EDGE,"E51"),sQuery(id+"F12.wireOp",EDGE,"E52"),sQuery(id+"F12.wireOp",EDGE,"E53"),sQuery(id+"F12.wireOp",EDGE,"E55"),sQuery(id+"F12.wireOp",EDGE,"E56"),sQuery(id+"F12.wireOp",EDGE,"E57"),sQuery(id+"F12.wireOp",EDGE,"E58"),sQuery(id+"F12.wireOp",EDGE,"E59"),sQuery(id+"F12.wireOp",EDGE,"E60.trimOffspring"),sQuery(id+"F12.wireOp",EDGE,"E61"),sQuery(id+"F12.wireOp",EDGE,"E62"),sQuery(id+"F12.wireOp",EDGE,"E64"),sQuery(id+"F12.wireOp",EDGE,"E65.trimOffspring"),sQuery(id+"F12.wireOp",EDGE,"E66"),sQuery(id+"F12.wireOp",EDGE,"E67"),sQuery(id+"F12.wireOp",EDGE,"E69"),sQuery(id+"F12.wireOp",EDGE,"E70.trimOffspring"),sQuery(id+"F12.wireOp",EDGE,"E72.0"),sQuery(id+"F12.wireOp",EDGE,"E72.1"),sQuery(id+"F12.wireOp",EDGE,"E72.2"),sQuery(id+"F12.wireOp",EDGE,"E72.3"),sQuery(id+"F12.wireOp",EDGE,"E73"),sQuery(id+"F12.wireOp",EDGE,"E74"),sQuery(id+"F12.wireOp",EDGE,"E75"),sQuery(id+"F12.wireOp",EDGE,"E77.filletArc"),sQuery(id+"F12.wireOp",EDGE,"E78.filletArc"),sQuery(id+"F12.wireOp",EDGE,"E79"),sQuery(id+"F12.wireOp",EDGE,"E80.filletArc"),sQuery(id+"F12.wireOp",EDGE,"E81.filletArc"),sQuery(id+"F12.wireOp",EDGE,"E83"),sQuery(id+"F12.wireOp",EDGE,"E84"),sQuery(id+"F12.wireOp",EDGE,"E85"),sQuery(id+"F12.wireOp",EDGE,"E86"),sQuery(id+"F12.wireOp",EDGE,"E87"),sQuery(id+"F12.wireOp",EDGE,"E90"),sQuery(id+"F12.wireOp",EDGE,"E91"),sQuery(id+"F12.wireOp",EDGE,"E92"),sQuery(id+"F12.wireOp",EDGE,"E93.trimOffspring"),sQuery(id+"F12.wireOp",EDGE,"E88")])],"isStart":false});
            var sketch = newSketch(context, id + "F27", { "sketchPlane" : qUnion([Q0])});
            skCircle(sketch, "E101", {"center": v(42.25, -42.25) * mm, "radius": 2.25 * mm});
            skSolve(sketch);
        }
        {
            var Q0;
            Q0 = qSketchRegion(id + "F27", true);
            extrude(context, id + "F28", {"entities" : qUnion([Q0]), "operationType" : NewBodyOperationType.REMOVE, "endBound" : BoundingType.THROUGH_ALL, "oppositeDirection" : true, "depth" : 25 * mm, "offsetDistance" : 25 * mm});
        }
        {
            var Q0;
            Q0=makeQuery(id+"F13.opExtrude","CAP_FACE",FACE,{"disambiguationData":[OSD([sQuery(id+"F12.wireOp",EDGE,"E48"),sQuery(id+"F12.wireOp",EDGE,"E50"),sQuery(id+"F12.wireOp",EDGE,"E51"),sQuery(id+"F12.wireOp",EDGE,"E52"),sQuery(id+"F12.wireOp",EDGE,"E53"),sQuery(id+"F12.wireOp",EDGE,"E55"),sQuery(id+"F12.wireOp",EDGE,"E56"),sQuery(id+"F12.wireOp",EDGE,"E57"),sQuery(id+"F12.wireOp",EDGE,"E58"),sQuery(id+"F12.wireOp",EDGE,"E59"),sQuery(id+"F12.wireOp",EDGE,"E60.trimOffspring"),sQuery(id+"F12.wireOp",EDGE,"E61"),sQuery(id+"F12.wireOp",EDGE,"E62"),sQuery(id+"F12.wireOp",EDGE,"E64"),sQuery(id+"F12.wireOp",EDGE,"E65.trimOffspring"),sQuery(id+"F12.wireOp",EDGE,"E66"),sQuery(id+"F12.wireOp",EDGE,"E67"),sQuery(id+"F12.wireOp",EDGE,"E69"),sQuery(id+"F12.wireOp",EDGE,"E70.trimOffspring"),sQuery(id+"F12.wireOp",EDGE,"E72.0"),sQuery(id+"F12.wireOp",EDGE,"E72.1"),sQuery(id+"F12.wireOp",EDGE,"E72.2"),sQuery(id+"F12.wireOp",EDGE,"E72.3"),sQuery(id+"F12.wireOp",EDGE,"E73"),sQuery(id+"F12.wireOp",EDGE,"E74"),sQuery(id+"F12.wireOp",EDGE,"E75"),sQuery(id+"F12.wireOp",EDGE,"E77.filletArc"),sQuery(id+"F12.wireOp",EDGE,"E78.filletArc"),sQuery(id+"F12.wireOp",EDGE,"E79"),sQuery(id+"F12.wireOp",EDGE,"E80.filletArc"),sQuery(id+"F12.wireOp",EDGE,"E81.filletArc"),sQuery(id+"F12.wireOp",EDGE,"E83"),sQuery(id+"F12.wireOp",EDGE,"E84"),sQuery(id+"F12.wireOp",EDGE,"E85"),sQuery(id+"F12.wireOp",EDGE,"E86"),sQuery(id+"F12.wireOp",EDGE,"E87"),sQuery(id+"F12.wireOp",EDGE,"E90"),sQuery(id+"F12.wireOp",EDGE,"E91"),sQuery(id+"F12.wireOp",EDGE,"E92"),sQuery(id+"F12.wireOp",EDGE,"E93.trimOffspring"),sQuery(id+"F12.wireOp",EDGE,"E88")])],"isStart":false});
            var sketch = newSketch(context, id + "F29", { "sketchPlane" : qUnion([Q0])});
            skCircle(sketch, "E102", {"center": v(36.77, -42.75) * mm, "radius": 1.75 * mm});
            skSolve(sketch);
        }
        {
            var Q0;
            Q0 = qSketchRegion(id + "F29", true);
            extrude(context, id + "F30", {"entities" : qUnion([Q0]), "operationType" : NewBodyOperationType.REMOVE, "oppositeDirection" : true, "depth" : 1 * mm, "offsetDistance" : 25 * mm});
        }
        {
            var Q0;
            Q0=makeQuery(id+"F13.opExtrude","CAP_FACE",FACE,{"disambiguationData":[OSD([sQuery(id+"F12.wireOp",EDGE,"E48"),sQuery(id+"F12.wireOp",EDGE,"E50"),sQuery(id+"F12.wireOp",EDGE,"E51"),sQuery(id+"F12.wireOp",EDGE,"E52"),sQuery(id+"F12.wireOp",EDGE,"E53"),sQuery(id+"F12.wireOp",EDGE,"E55"),sQuery(id+"F12.wireOp",EDGE,"E56"),sQuery(id+"F12.wireOp",EDGE,"E57"),sQuery(id+"F12.wireOp",EDGE,"E58"),sQuery(id+"F12.wireOp",EDGE,"E59"),sQuery(id+"F12.wireOp",EDGE,"E60.trimOffspring"),sQuery(id+"F12.wireOp",EDGE,"E61"),sQuery(id+"F12.wireOp",EDGE,"E62"),sQuery(id+"F12.wireOp",EDGE,"E64"),sQuery(id+"F12.wireOp",EDGE,"E65.trimOffspring"),sQuery(id+"F12.wireOp",EDGE,"E66"),sQuery(id+"F12.wireOp",EDGE,"E67"),sQuery(id+"F12.wireOp",EDGE,"E69"),sQuery(id+"F12.wireOp",EDGE,"E70.trimOffspring"),sQuery(id+"F12.wireOp",EDGE,"E72.0"),sQuery(id+"F12.wireOp",EDGE,"E72.1"),sQuery(id+"F12.wireOp",EDGE,"E72.2"),sQuery(id+"F12.wireOp",EDGE,"E72.3"),sQuery(id+"F12.wireOp",EDGE,"E73"),sQuery(id+"F12.wireOp",EDGE,"E74"),sQuery(id+"F12.wireOp",EDGE,"E75"),sQuery(id+"F12.wireOp",EDGE,"E77.filletArc"),sQuery(id+"F12.wireOp",EDGE,"E78.filletArc"),sQuery(id+"F12.wireOp",EDGE,"E79"),sQuery(id+"F12.wireOp",EDGE,"E80.filletArc"),sQuery(id+"F12.wireOp",EDGE,"E81.filletArc"),sQuery(id+"F12.wireOp",EDGE,"E83"),sQuery(id+"F12.wireOp",EDGE,"E84"),sQuery(id+"F12.wireOp",EDGE,"E85"),sQuery(id+"F12.wireOp",EDGE,"E86"),sQuery(id+"F12.wireOp",EDGE,"E87"),sQuery(id+"F12.wireOp",EDGE,"E90"),sQuery(id+"F12.wireOp",EDGE,"E91"),sQuery(id+"F12.wireOp",EDGE,"E92"),sQuery(id+"F12.wireOp",EDGE,"E93.trimOffspring"),sQuery(id+"F12.wireOp",EDGE,"E88")])],"isStart":false});
            var sketch = newSketch(context, id + "F31", { "sketchPlane" : qUnion([Q0])});
            skCircle(sketch, "E103", {"center": v(42.75, -36.77) * mm, "radius": 1.75 * mm});
            skSolve(sketch);
        }
        {
            var Q0;
            Q0 = qSketchRegion(id + "F31", true);
            extrude(context, id + "F32", {"entities" : qUnion([Q0]), "operationType" : NewBodyOperationType.REMOVE, "oppositeDirection" : true, "depth" : 1 * mm, "offsetDistance" : 25 * mm});
        }
        {
            var Q0;
            Q0=makeQuery(id+"F13.opExtrude","CAP_FACE",FACE,{"disambiguationData":[OSD([sQuery(id+"F12.wireOp",EDGE,"E48"),sQuery(id+"F12.wireOp",EDGE,"E50"),sQuery(id+"F12.wireOp",EDGE,"E51"),sQuery(id+"F12.wireOp",EDGE,"E52"),sQuery(id+"F12.wireOp",EDGE,"E53"),sQuery(id+"F12.wireOp",EDGE,"E55"),sQuery(id+"F12.wireOp",EDGE,"E56"),sQuery(id+"F12.wireOp",EDGE,"E57"),sQuery(id+"F12.wireOp",EDGE,"E58"),sQuery(id+"F12.wireOp",EDGE,"E59"),sQuery(id+"F12.wireOp",EDGE,"E60.trimOffspring"),sQuery(id+"F12.wireOp",EDGE,"E61"),sQuery(id+"F12.wireOp",EDGE,"E62"),sQuery(id+"F12.wireOp",EDGE,"E64"),sQuery(id+"F12.wireOp",EDGE,"E65.trimOffspring"),sQuery(id+"F12.wireOp",EDGE,"E66"),sQuery(id+"F12.wireOp",EDGE,"E67"),sQuery(id+"F12.wireOp",EDGE,"E69"),sQuery(id+"F12.wireOp",EDGE,"E70.trimOffspring"),sQuery(id+"F12.wireOp",EDGE,"E72.0"),sQuery(id+"F12.wireOp",EDGE,"E72.1"),sQuery(id+"F12.wireOp",EDGE,"E72.2"),sQuery(id+"F12.wireOp",EDGE,"E72.3"),sQuery(id+"F12.wireOp",EDGE,"E73"),sQuery(id+"F12.wireOp",EDGE,"E74"),sQuery(id+"F12.wireOp",EDGE,"E75"),sQuery(id+"F12.wireOp",EDGE,"E77.filletArc"),sQuery(id+"F12.wireOp",EDGE,"E78.filletArc"),sQuery(id+"F12.wireOp",EDGE,"E79"),sQuery(id+"F12.wireOp",EDGE,"E80.filletArc"),sQuery(id+"F12.wireOp",EDGE,"E81.filletArc"),sQuery(id+"F12.wireOp",EDGE,"E83"),sQuery(id+"F12.wireOp",EDGE,"E84"),sQuery(id+"F12.wireOp",EDGE,"E85"),sQuery(id+"F12.wireOp",EDGE,"E86"),sQuery(id+"F12.wireOp",EDGE,"E87"),sQuery(id+"F12.wireOp",EDGE,"E90"),sQuery(id+"F12.wireOp",EDGE,"E91"),sQuery(id+"F12.wireOp",EDGE,"E92"),sQuery(id+"F12.wireOp",EDGE,"E93.trimOffspring"),sQuery(id+"F12.wireOp",EDGE,"E88")])],"isStart":false});
            var sketch = newSketch(context, id + "F33", { "sketchPlane" : qUnion([Q0])});
            skCircle(sketch, "E104", {"center": v(41.75, 41.52) * mm, "radius": 2.25 * mm});
            skSolve(sketch);
        }
        {
            var Q0;
            Q0 = qSketchRegion(id + "F33", true);
            extrude(context, id + "F34", {"entities" : qUnion([Q0]), "operationType" : NewBodyOperationType.REMOVE, "endBound" : BoundingType.THROUGH_ALL, "oppositeDirection" : true, "depth" : 25 * mm, "offsetDistance" : 25 * mm});
        }
        {
            var Q0;
            Q0=makeQuery(id+"F13.opExtrude","CAP_FACE",FACE,{"disambiguationData":[OSD([sQuery(id+"F12.wireOp",EDGE,"E48"),sQuery(id+"F12.wireOp",EDGE,"E50"),sQuery(id+"F12.wireOp",EDGE,"E51"),sQuery(id+"F12.wireOp",EDGE,"E52"),sQuery(id+"F12.wireOp",EDGE,"E53"),sQuery(id+"F12.wireOp",EDGE,"E55"),sQuery(id+"F12.wireOp",EDGE,"E56"),sQuery(id+"F12.wireOp",EDGE,"E57"),sQuery(id+"F12.wireOp",EDGE,"E58"),sQuery(id+"F12.wireOp",EDGE,"E59"),sQuery(id+"F12.wireOp",EDGE,"E60.trimOffspring"),sQuery(id+"F12.wireOp",EDGE,"E61"),sQuery(id+"F12.wireOp",EDGE,"E62"),sQuery(id+"F12.wireOp",EDGE,"E64"),sQuery(id+"F12.wireOp",EDGE,"E65.trimOffspring"),sQuery(id+"F12.wireOp",EDGE,"E66"),sQuery(id+"F12.wireOp",EDGE,"E67"),sQuery(id+"F12.wireOp",EDGE,"E69"),sQuery(id+"F12.wireOp",EDGE,"E70.trimOffspring"),sQuery(id+"F12.wireOp",EDGE,"E72.0"),sQuery(id+"F12.wireOp",EDGE,"E72.1"),sQuery(id+"F12.wireOp",EDGE,"E72.2"),sQuery(id+"F12.wireOp",EDGE,"E72.3"),sQuery(id+"F12.wireOp",EDGE,"E73"),sQuery(id+"F12.wireOp",EDGE,"E74"),sQuery(id+"F12.wireOp",EDGE,"E75"),sQuery(id+"F12.wireOp",EDGE,"E77.filletArc"),sQuery(id+"F12.wireOp",EDGE,"E78.filletArc"),sQuery(id+"F12.wireOp",EDGE,"E79"),sQuery(id+"F12.wireOp",EDGE,"E80.filletArc"),sQuery(id+"F12.wireOp",EDGE,"E81.filletArc"),sQuery(id+"F12.wireOp",EDGE,"E83"),sQuery(id+"F12.wireOp",EDGE,"E84"),sQuery(id+"F12.wireOp",EDGE,"E85"),sQuery(id+"F12.wireOp",EDGE,"E86"),sQuery(id+"F12.wireOp",EDGE,"E87"),sQuery(id+"F12.wireOp",EDGE,"E90"),sQuery(id+"F12.wireOp",EDGE,"E91"),sQuery(id+"F12.wireOp",EDGE,"E92"),sQuery(id+"F12.wireOp",EDGE,"E93.trimOffspring"),sQuery(id+"F12.wireOp",EDGE,"E88")])],"isStart":false});
            var sketch = newSketch(context, id + "F35", { "sketchPlane" : qUnion([Q0])});
            skCircle(sketch, "E105", {"center": v(36.4, 42.77) * mm, "radius": 1.75 * mm});
            skSolve(sketch);
        }
        {
            var Q0;
            Q0 = qSketchRegion(id + "F35", true);
            extrude(context, id + "F36", {"entities" : qUnion([Q0]), "operationType" : NewBodyOperationType.REMOVE, "oppositeDirection" : true, "depth" : 1 * mm, "offsetDistance" : 25 * mm});
        }
        {
            var Q0;
            Q0=makeQuery(id+"F13.opExtrude","CAP_FACE",FACE,{"disambiguationData":[OSD([sQuery(id+"F12.wireOp",EDGE,"E48"),sQuery(id+"F12.wireOp",EDGE,"E50"),sQuery(id+"F12.wireOp",EDGE,"E51"),sQuery(id+"F12.wireOp",EDGE,"E52"),sQuery(id+"F12.wireOp",EDGE,"E53"),sQuery(id+"F12.wireOp",EDGE,"E55"),sQuery(id+"F12.wireOp",EDGE,"E56"),sQuery(id+"F12.wireOp",EDGE,"E57"),sQuery(id+"F12.wireOp",EDGE,"E58"),sQuery(id+"F12.wireOp",EDGE,"E59"),sQuery(id+"F12.wireOp",EDGE,"E60.trimOffspring"),sQuery(id+"F12.wireOp",EDGE,"E61"),sQuery(id+"F12.wireOp",EDGE,"E62"),sQuery(id+"F12.wireOp",EDGE,"E64"),sQuery(id+"F12.wireOp",EDGE,"E65.trimOffspring"),sQuery(id+"F12.wireOp",EDGE,"E66"),sQuery(id+"F12.wireOp",EDGE,"E67"),sQuery(id+"F12.wireOp",EDGE,"E69"),sQuery(id+"F12.wireOp",EDGE,"E70.trimOffspring"),sQuery(id+"F12.wireOp",EDGE,"E72.0"),sQuery(id+"F12.wireOp",EDGE,"E72.1"),sQuery(id+"F12.wireOp",EDGE,"E72.2"),sQuery(id+"F12.wireOp",EDGE,"E72.3"),sQuery(id+"F12.wireOp",EDGE,"E73"),sQuery(id+"F12.wireOp",EDGE,"E74"),sQuery(id+"F12.wireOp",EDGE,"E75"),sQuery(id+"F12.wireOp",EDGE,"E77.filletArc"),sQuery(id+"F12.wireOp",EDGE,"E78.filletArc"),sQuery(id+"F12.wireOp",EDGE,"E79"),sQuery(id+"F12.wireOp",EDGE,"E80.filletArc"),sQuery(id+"F12.wireOp",EDGE,"E81.filletArc"),sQuery(id+"F12.wireOp",EDGE,"E83"),sQuery(id+"F12.wireOp",EDGE,"E84"),sQuery(id+"F12.wireOp",EDGE,"E85"),sQuery(id+"F12.wireOp",EDGE,"E86"),sQuery(id+"F12.wireOp",EDGE,"E87"),sQuery(id+"F12.wireOp",EDGE,"E90"),sQuery(id+"F12.wireOp",EDGE,"E91"),sQuery(id+"F12.wireOp",EDGE,"E92"),sQuery(id+"F12.wireOp",EDGE,"E93.trimOffspring"),sQuery(id+"F12.wireOp",EDGE,"E88")])],"isStart":false});
            var sketch = newSketch(context, id + "F37", { "sketchPlane" : qUnion([Q0])});
            skCircle(sketch, "E106", {"center": v(42.75, 36.12) * mm, "radius": 1.75 * mm});
            skSolve(sketch);
        }
        {
            var Q0;
            Q0 = qSketchRegion(id + "F37", true);
            extrude(context, id + "F38", {"entities" : qUnion([Q0]), "operationType" : NewBodyOperationType.REMOVE, "oppositeDirection" : true, "depth" : 1 * mm, "offsetDistance" : 25 * mm});
        }
        {
            var Q0;
            Q0=qCreatedBy(id+"F11.planeOp",FACE);
            cPlane(context, id + "F39", {"entities" : qUnion([Q0]), "cplaneType" : CPlaneType.OFFSET, "offset" : 23 * mm, "width" : 150 * mm, "height" : 150 * mm});
        }
        {
            var Q0;
            Q0=qCreatedBy(id+"F39.planeOp",FACE);
            var sketch = newSketch(context, id + "F40", { "sketchPlane" : qUnion([Q0])});
            skLineSegment(sketch, "E107", {"start": v(0, 0) * mm, "end": v(-46, 0) * mm});
            skLineSegment(sketch, "E108", {"start": v(0, 0) * mm, "end": v(0, -46) * mm});
            skLineSegment(sketch, "E109", {"start": v(0, 0) * mm, "end": v(46, 0) * mm});
            skLineSegment(sketch, "E110", {"start": v(0, 0) * mm, "end": v(0, 46) * mm});
            skLineSegment(sketch, "E111", {"start": v(-46, 0) * mm, "end": v(-46, -44) * mm});
            skLineSegment(sketch, "E112", {"start": v(-44, -46) * mm, "end": v(44, -46) * mm});
            skLineSegment(sketch, "E113", {"start": v(46, -44) * mm, "end": v(46, 43.5) * mm});
            skLineSegment(sketch, "E114", {"start": v(0, 46) * mm, "end": v(-44, 46) * mm});
            skLineSegment(sketch, "E115", {"start": v(-46, 44) * mm, "end": v(-46, 0) * mm});
            skPoint(sketch, "E116.visualSharp", {"position": v(-46, -46) * mm});
            skArc(sketch, "E116.filletArc", {"start": v(-46, -44) * mm, "mid": v(-45.41, -45.41) * mm, "end": v(-44, -46) * mm});
            skPoint(sketch, "E117.visualSharp", {"position": v(-46, 46) * mm});
            skArc(sketch, "E117.filletArc", {"start": v(-44, 46) * mm, "mid": v(-45.41, 45.41) * mm, "end": v(-46, 44) * mm});
            skPoint(sketch, "E118.visualSharp", {"position": v(46, -46) * mm});
            skArc(sketch, "E118.filletArc", {"start": v(44, -46) * mm, "mid": v(45.41, -45.41) * mm, "end": v(46, -44) * mm});
            skPoint(sketch, "E119.visualSharp", {"position": v(46, 46) * mm});
            skLineSegment(sketch, "E120.0", {"start": v(-44.5, 29.56) * mm, "end": v(-44.5, -0.03) * mm});
            skLineSegment(sketch, "E121.0", {"start": v(-44.5, -0.03) * mm, "end": v(-44.5, -29.05) * mm});
            skLineSegment(sketch, "E122.0", {"start": v(29.44, 44.5) * mm, "end": v(-28.78, 44.5) * mm});
            skLineSegment(sketch, "E123.0", {"start": v(-29.18, -44.5) * mm, "end": v(28.34, -44.5) * mm});
            skLineSegment(sketch, "E124.0", {"start": v(44.5, -27.94) * mm, "end": v(44.5, 28.78) * mm});
            skLineSegment(sketch, "E125", {"start": v(0, 46) * mm, "end": v(43.86, 46) * mm});
            skFitSpline(sketch, "E126", {"points": [v(43.86, 46) * mm, v(46, 43.5) * mm], "startDerivative": vector(5.11, 0.04) * mm, "endDerivative": vector(-0.3, -3.68) * mm});
            skLineSegment(sketch, "E127", {"start": v(-46, -44) * mm, "end": v(-46, -26) * mm});
            skLineSegment(sketch, "E128", {"start": v(-44, -46) * mm, "end": v(-26, -46) * mm});
            skLineSegment(sketch, "E129", {"start": v(-46, 44) * mm, "end": v(-46, 26) * mm});
            skLineSegment(sketch, "E130", {"start": v(-44, 46) * mm, "end": v(-26, 46) * mm});
            skLineSegment(sketch, "E131", {"start": v(44, -46) * mm, "end": v(26, -46) * mm});
            skLineSegment(sketch, "E132", {"start": v(46, -44) * mm, "end": v(46, -26) * mm});
            skLineSegment(sketch, "E133", {"start": v(43.91, 46) * mm, "end": v(26, 46) * mm});
            skLineSegment(sketch, "E134", {"start": v(46, 44.05) * mm, "end": v(46, 26) * mm});
            skFitSpline(sketch, "E135", {"points": [v(-46, -26) * mm, v(-26, -46) * mm], "startDerivative": vector(12.64, -28.52) * mm, "endDerivative": vector(25.65, -10.57) * mm});
            skFitSpline(sketch, "E136", {"points": [v(-46, 26) * mm, v(-26, 46) * mm], "startDerivative": vector(12.2, 35.3) * mm, "endDerivative": vector(18.1, 9.68) * mm});
            skFitSpline(sketch, "E137", {"points": [v(26, -46) * mm, v(46, -26) * mm], "startDerivative": vector(26.6, 15.88) * mm, "endDerivative": vector(15.87, 20.5) * mm});
            skFitSpline(sketch, "E138", {"points": [v(46, 26) * mm, v(26, 46) * mm], "startDerivative": vector(-11.93, 22.77) * mm, "endDerivative": vector(-33.04, 12.19) * mm});
            skSolve(sketch);
        }
        {
            var Q0;
            Q0 = qSketchRegion(id + "F40", true);
            extrude(context, id + "F41", {"entities" : qUnion([Q0]), "depth" : 5 * mm, "offsetDistance" : 25 * mm});
        }
        {
            var Q0;
            Q0=makeQuery(id+"F41.opExtrude","CAP_FACE",FACE,{"disambiguationData":[OSD([sQuery(id+"F40.wireOp",EDGE,"E111"),sQuery(id+"F40.wireOp",EDGE,"E112"),sQuery(id+"F40.wireOp",EDGE,"E113"),sQuery(id+"F40.wireOp",EDGE,"E114"),sQuery(id+"F40.wireOp",EDGE,"E115"),sQuery(id+"F40.wireOp",EDGE,"E116.filletArc"),sQuery(id+"F40.wireOp",EDGE,"E117.filletArc"),sQuery(id+"F40.wireOp",EDGE,"E118.filletArc"),sQuery(id+"F40.wireOp",EDGE,"E120.0"),sQuery(id+"F40.wireOp",EDGE,"E121.0"),sQuery(id+"F40.wireOp",EDGE,"E122.0"),sQuery(id+"F40.wireOp",EDGE,"E123.0"),sQuery(id+"F40.wireOp",EDGE,"E124.0"),sQuery(id+"F40.wireOp",EDGE,"E125"),sQuery(id+"F40.wireOp",EDGE,"E126"),sQuery(id+"F40.wireOp",EDGE,"E127"),sQuery(id+"F40.wireOp",EDGE,"E128"),sQuery(id+"F40.wireOp",EDGE,"E129"),sQuery(id+"F40.wireOp",EDGE,"E130"),sQuery(id+"F40.wireOp",EDGE,"E131"),sQuery(id+"F40.wireOp",EDGE,"E132"),sQuery(id+"F40.wireOp",EDGE,"E133"),sQuery(id+"F40.wireOp",EDGE,"E134"),sQuery(id+"F40.wireOp",EDGE,"E135"),sQuery(id+"F40.wireOp",EDGE,"E136"),sQuery(id+"F40.wireOp",EDGE,"E137"),sQuery(id+"F40.wireOp",EDGE,"E138")])],"isStart":true});
            var sketch = newSketch(context, id + "F42", { "sketchPlane" : qUnion([Q0])});
            skCircle(sketch, "E139", {"center": v(0, 0) * mm, "radius": 46 * mm});
            skCircle(sketch, "E140", {"center": v(0, 0) * mm, "radius": 44.5 * mm});
            skSolve(sketch);
        }
        {
            var Q0;
            Q0 = qSketchRegion(id + "F42", true);
            extrude(context, id + "F43", {"entities" : qUnion([Q0]), "depth" : 23 * mm, "offsetDistance" : 25 * mm});
        }
        {
            var Q0;
            Q0=makeQuery(id+"F41.opExtrude","CAP_FACE",FACE,{"disambiguationData":[OSD([sQuery(id+"F40.wireOp",EDGE,"E111"),sQuery(id+"F40.wireOp",EDGE,"E112"),sQuery(id+"F40.wireOp",EDGE,"E113"),sQuery(id+"F40.wireOp",EDGE,"E114"),sQuery(id+"F40.wireOp",EDGE,"E115"),sQuery(id+"F40.wireOp",EDGE,"E116.filletArc"),sQuery(id+"F40.wireOp",EDGE,"E117.filletArc"),sQuery(id+"F40.wireOp",EDGE,"E118.filletArc"),sQuery(id+"F40.wireOp",EDGE,"E120.0"),sQuery(id+"F40.wireOp",EDGE,"E121.0"),sQuery(id+"F40.wireOp",EDGE,"E122.0"),sQuery(id+"F40.wireOp",EDGE,"E123.0"),sQuery(id+"F40.wireOp",EDGE,"E124.0"),sQuery(id+"F40.wireOp",EDGE,"E125"),sQuery(id+"F40.wireOp",EDGE,"E126"),sQuery(id+"F40.wireOp",EDGE,"E127"),sQuery(id+"F40.wireOp",EDGE,"E128"),sQuery(id+"F40.wireOp",EDGE,"E129"),sQuery(id+"F40.wireOp",EDGE,"E130"),sQuery(id+"F40.wireOp",EDGE,"E131"),sQuery(id+"F40.wireOp",EDGE,"E132"),sQuery(id+"F40.wireOp",EDGE,"E133"),sQuery(id+"F40.wireOp",EDGE,"E134"),sQuery(id+"F40.wireOp",EDGE,"E135"),sQuery(id+"F40.wireOp",EDGE,"E136"),sQuery(id+"F40.wireOp",EDGE,"E137"),sQuery(id+"F40.wireOp",EDGE,"E138")])],"isStart":false});
            var sketch = newSketch(context, id + "F44", { "sketchPlane" : qUnion([Q0])});
            skCircle(sketch, "E141", {"center": v(-42.3, -42.3) * mm, "radius": 3.5 * mm});
            skCircle(sketch, "E142", {"center": v(-42.3, 42.3) * mm, "radius": 3.5 * mm});
            skCircle(sketch, "E143", {"center": v(42.3, 42.3) * mm, "radius": 3.5 * mm});
            skCircle(sketch, "E144", {"center": v(42.3, -42.3) * mm, "radius": 3.5 * mm});
            skPoint(sketch, "E145", {"position": v(45.8, -42.34) * mm});
            skPoint(sketch, "E146", {"position": v(46, -42.35) * mm});
            skSolve(sketch);
        }
        {
            var Q0;
            Q0 = qSketchRegion(id + "F44", true);
            extrude(context, id + "F45", {"entities" : qUnion([Q0]), "operationType" : NewBodyOperationType.ADD, "depth" : 3 * mm, "offsetDistance" : 25 * mm});
        }
        {
            var Q0;
            Q0=qCreatedBy(id+"F39.planeOp",FACE);
            cPlane(context, id + "F46", {"entities" : qUnion([Q0]), "cplaneType" : CPlaneType.OFFSET, "offset" : 7 * mm, "width" : 150 * mm, "height" : 150 * mm});
        }
        {
            var Q0;
            Q0=qCreatedBy(id+"F46.planeOp",FACE);
            var sketch = newSketch(context, id + "F47", { "sketchPlane" : qUnion([Q0])});
            skCircle(sketch, "E147", {"center": v(0, 0) * mm, "radius": 7 * mm});
            skCircle(sketch, "E148.0", {"center": v(0, 0) * mm, "radius": 8 * mm});
            skCircle(sketch, "E149", {"center": v(0, 0) * mm, "radius": 14.5 * mm});
            skCircle(sketch, "E150.0", {"center": v(0, 0) * mm, "radius": 15.5 * mm});
            skCircle(sketch, "E151", {"center": v(0, 0) * mm, "radius": 23 * mm});
            skCircle(sketch, "E152.0", {"center": v(0, 0) * mm, "radius": 22 * mm});
            skCircle(sketch, "E153", {"center": v(0, 0) * mm, "radius": 30.5 * mm});
            skCircle(sketch, "E154.0", {"center": v(0, 0) * mm, "radius": 29.5 * mm});
            skCircle(sketch, "E155", {"center": v(0, 0) * mm, "radius": 37.5 * mm});
            skCircle(sketch, "E156.0", {"center": v(0, 0) * mm, "radius": 36.5 * mm});
            skCircle(sketch, "E157", {"center": v(0, 0) * mm, "radius": 44.5 * mm});
            skCircle(sketch, "E158.0", {"center": v(0, 0) * mm, "radius": 43.5 * mm});
            skSolve(sketch);
        }
        {
            var Q0;
            Q0 = qSketchRegion(id + "F47", true);
            var Q1;
            Q1=makeQuery(id+"F47.imprint","IMPRINT",FACE,{"disambiguationData":[TD([[makeQuery(id+"F47.imprint","IMPRINT",EDGE,{"derivedFrom":sQuery(id+"F47.wireOp",EDGE,"E151")}),1.0]])]});
            var Q2;
            Q2=makeQuery(id+"F47.imprint","IMPRINT",FACE,{"disambiguationData":[TD([[makeQuery(id+"F47.imprint","IMPRINT",EDGE,{"derivedFrom":sQuery(id+"F47.wireOp",EDGE,"E149")}),-1.0]])]});
            var Q3;
            Q3=makeQuery(id+"F47.imprint","IMPRINT",FACE,{"disambiguationData":[TD([[makeQuery(id+"F47.imprint","IMPRINT",EDGE,{"derivedFrom":sQuery(id+"F47.wireOp",EDGE,"E147")}),-1.0]])]});
            var Q4;
            Q4=makeQuery(id+"F47.imprint","IMPRINT",FACE,{"disambiguationData":[TD([[makeQuery(id+"F47.imprint","IMPRINT",EDGE,{"derivedFrom":sQuery(id+"F47.wireOp",EDGE,"E153")}),1.0]])]});
            var Q5;
            Q5=makeQuery(id+"F47.imprint","IMPRINT",FACE,{"disambiguationData":[TD([[makeQuery(id+"F47.imprint","IMPRINT",EDGE,{"derivedFrom":sQuery(id+"F47.wireOp",EDGE,"E155")}),1.0]])]});
            extrude(context, id + "F48", {"entities" : qUnion([Q0, Q1, Q2, Q3, Q4, Q5]), "depth" : 1 * mm, "offsetDistance" : 25 * mm});
        }
        {
            var Q0;
            Q0=makeQuery(id+"F45.opExtrude","CAP_FACE",FACE,{"disambiguationData":[OSD([sQuery(id+"F44.wireOp",EDGE,"E142")])],"isStart":false});
            var sketch = newSketch(context, id + "F49", { "sketchPlane" : qUnion([Q0])});
            skPoint(sketch, "E159.visualSharp", {"position": v(0, 0) * mm});
            skLineSegment(sketch, "E160.0", {"start": v(3.53, 2.84) * mm, "end": v(39.95, 39.45) * mm});
            skLineSegment(sketch, "E160.1", {"start": v(3.54, -2.82) * mm, "end": v(40.18, -39.27) * mm});
            skPoint(sketch, "E161.visualSharp", {"position": v(0.7, 0) * mm});
            skArc(sketch, "E161.filletArc", {"start": v(3.53, 2.84) * mm, "mid": v(2.36, 0) * mm, "end": v(3.54, -2.82) * mm});
            skLineSegment(sketch, "E162.0", {"start": v(2.47, 3.19) * mm, "end": v(39.24, 40.15) * mm});
            skArc(sketch, "E162.1", {"start": v(2.47, 3.19) * mm, "mid": v(1.16, 0) * mm, "end": v(2.48, -3.18) * mm});
            skLineSegment(sketch, "E162.2", {"start": v(2.48, -3.18) * mm, "end": v(39.48, -39.98) * mm});
            skPoint(sketch, "E163.visualSharp", {"position": v(-0.7, 0) * mm});
            skArc(sketch, "E163.filletArc", {"start": v(-3.53, -2.84) * mm, "mid": v(-2.36, 0) * mm, "end": v(-3.54, 2.82) * mm});
            skArc(sketch, "E164.1", {"start": v(-2.47, -3.19) * mm, "mid": v(-1.16, 0) * mm, "end": v(-2.48, 3.18) * mm});
            skLineSegment(sketch, "E165", {"start": v(40.18, -39.27) * mm, "end": v(40.34, -39.42) * mm});
            skLineSegment(sketch, "E166", {"start": v(40.34, -39.42) * mm, "end": v(39.68, -40.11) * mm});
            skLineSegment(sketch, "E167", {"start": v(39.48, -39.98) * mm, "end": v(39.68, -40.18) * mm});
            skLineSegment(sketch, "E168", {"start": v(39.68, -40.18) * mm, "end": v(39.68, -40.11) * mm});
            skLineSegment(sketch, "E169", {"start": v(39.24, 40.15) * mm, "end": v(39.95, 40.95) * mm});
            skLineSegment(sketch, "E170", {"start": v(39.95, 40.95) * mm, "end": v(40.84, 40.15) * mm});
            skLineSegment(sketch, "E171", {"start": v(40.84, 40.15) * mm, "end": v(39.95, 39.45) * mm});
            skPoint(sketch, "E172.end.orphan", {"position": v(-39.74, 40.24) * mm});
            skLineSegment(sketch, "E173", {"start": v(-2.48, 3.18) * mm, "end": v(-41.73, 42.23) * mm});
            skLineSegment(sketch, "E174", {"start": v(-3.54, 2.82) * mm, "end": v(-42.42, 41.5) * mm});
            skLineSegment(sketch, "E175", {"start": v(-42.42, 41.5) * mm, "end": v(-41.73, 42.23) * mm});
            skPoint(sketch, "E176.end.orphan", {"position": v(-39.74, -40.62) * mm});
            skPoint(sketch, "E177.end.orphan", {"position": v(-39.74, -40.66) * mm});
            skLineSegment(sketch, "E178", {"start": v(-3.53, -2.84) * mm, "end": v(-42.45, -41.96) * mm});
            skLineSegment(sketch, "E179", {"start": v(-2.47, -3.19) * mm, "end": v(-41.75, -42.67) * mm});
            skLineSegment(sketch, "E180", {"start": v(-41.75, -42.67) * mm, "end": v(-42.45, -41.96) * mm});
            skSolve(sketch);
        }
        {
            var Q0;
            Q0 = qSketchRegion(id + "F49", true);
            extrude(context, id + "F50", {"entities" : qUnion([Q0]), "depth" : 1 * mm, "offsetDistance" : 25 * mm});
        }
        {
            var Q0;
            Q0 = qSketchRegion(id + "F49", true);
            extrude(context, id + "F51", {"entities" : qUnion([Q0]), "depth" : 1 * mm, "offsetDistance" : 25 * mm});
        }
        {
            var Q0;
            {var subQ0=sQuery(id+"F2.wireOp",EDGE,"E24");var subQ8=makeQuery(id+"F2.imprint","INTERSECT",VERTEX,{"derivedFrom":[subQ0,sQuery(id+"F2.wireOp",EDGE,"E30")]});Q0=makeQuery(id+"F2.imprint","IMPRINT",FACE,{"disambiguationData":[TD([[makeQuery(id+"F2.imprint","IMPRINT",EDGE,{"disambiguationData":[TD([[subQ8,1.0]])],"derivedFrom":subQ0}),1.0]])]});}
            var sketch = newSketch(context, id + "F52", { "sketchPlane" : qUnion([Q0])});
            skCircle(sketch, "E181", {"center": v(0, 0) * mm, "radius": 1.94 * mm});
            skSolve(sketch);
        }
        {
            var Q0;
            Q0 = qSketchRegion(id + "F52", true);
            extrude(context, id + "F53", {"entities" : qUnion([Q0]), "operationType" : NewBodyOperationType.ADD, "depth" : 13 * mm, "offsetDistance" : 25 * mm, "hasSecondDirection" : true, "secondDirectionOppositeDirection" : true, "secondDirectionDepth" : 20 * mm});
        }
        {
            var Q0;
            Q0=makeQuery(id+"F45.opExtrude","CAP_FACE",FACE,{"disambiguationData":[OSD([sQuery(id+"F44.wireOp",EDGE,"E143")])],"isStart":false});
            var sketch = newSketch(context, id + "F54", { "sketchPlane" : qUnion([Q0])});
            skCircle(sketch, "E182", {"center": v(42.3, 42.3) * mm, "radius": 1.83 * mm});
            skSolve(sketch);
        }
        {
            var Q0;
            Q0 = qSketchRegion(id + "F54", true);
            extrude(context, id + "F55", {"entities" : qUnion([Q0]), "operationType" : NewBodyOperationType.ADD, "depth" : 2 * mm, "offsetDistance" : 25 * mm, "hasSecondDirection" : true, "secondDirectionOppositeDirection" : true, "secondDirectionDepth" : 37 * mm});
        }
        {
            var Q0;
            Q0=makeQuery(id+"F41.opExtrude","CAP_FACE",FACE,{"disambiguationData":[OSD([sQuery(id+"F40.wireOp",EDGE,"E111"),sQuery(id+"F40.wireOp",EDGE,"E112"),sQuery(id+"F40.wireOp",EDGE,"E113"),sQuery(id+"F40.wireOp",EDGE,"E114"),sQuery(id+"F40.wireOp",EDGE,"E115"),sQuery(id+"F40.wireOp",EDGE,"E116.filletArc"),sQuery(id+"F40.wireOp",EDGE,"E117.filletArc"),sQuery(id+"F40.wireOp",EDGE,"E118.filletArc"),sQuery(id+"F40.wireOp",EDGE,"E120.0"),sQuery(id+"F40.wireOp",EDGE,"E121.0"),sQuery(id+"F40.wireOp",EDGE,"E122.0"),sQuery(id+"F40.wireOp",EDGE,"E123.0"),sQuery(id+"F40.wireOp",EDGE,"E124.0"),sQuery(id+"F40.wireOp",EDGE,"E125"),sQuery(id+"F40.wireOp",EDGE,"E126"),sQuery(id+"F40.wireOp",EDGE,"E127"),sQuery(id+"F40.wireOp",EDGE,"E128"),sQuery(id+"F40.wireOp",EDGE,"E129"),sQuery(id+"F40.wireOp",EDGE,"E130"),sQuery(id+"F40.wireOp",EDGE,"E131"),sQuery(id+"F40.wireOp",EDGE,"E132"),sQuery(id+"F40.wireOp",EDGE,"E133"),sQuery(id+"F40.wireOp",EDGE,"E134"),sQuery(id+"F40.wireOp",EDGE,"E135"),sQuery(id+"F40.wireOp",EDGE,"E136"),sQuery(id+"F40.wireOp",EDGE,"E137"),sQuery(id+"F40.wireOp",EDGE,"E138")])],"isStart":false});
            var sketch = newSketch(context, id + "F56", { "sketchPlane" : qUnion([Q0])});
            skLineSegment(sketch, "E183.bottom", {"start": v(-44.5, 6.23) * mm, "end": v(44.5, 6.23) * mm});
            skLineSegment(sketch, "E183.top", {"start": v(-44.5, 4.98) * mm, "end": v(44.5, 4.98) * mm});
            skLineSegment(sketch, "E183.left", {"start": v(-44.5, 6.23) * mm, "end": v(-44.5, 4.98) * mm});
            skLineSegment(sketch, "E183.right", {"start": v(44.5, 6.23) * mm, "end": v(44.5, 4.98) * mm});
            skSolve(sketch);
        }
        {
            var Q0;
            Q0 = qSketchRegion(id + "F56", true);
            extrude(context, id + "F57", {"entities" : qUnion([Q0]), "operationType" : NewBodyOperationType.ADD, "depth" : 5 * mm, "offsetDistance" : 25 * mm, "hasSecondDirection" : true, "secondDirectionOppositeDirection" : true, "secondDirectionDepth" : 35 * mm});
        }
    });
